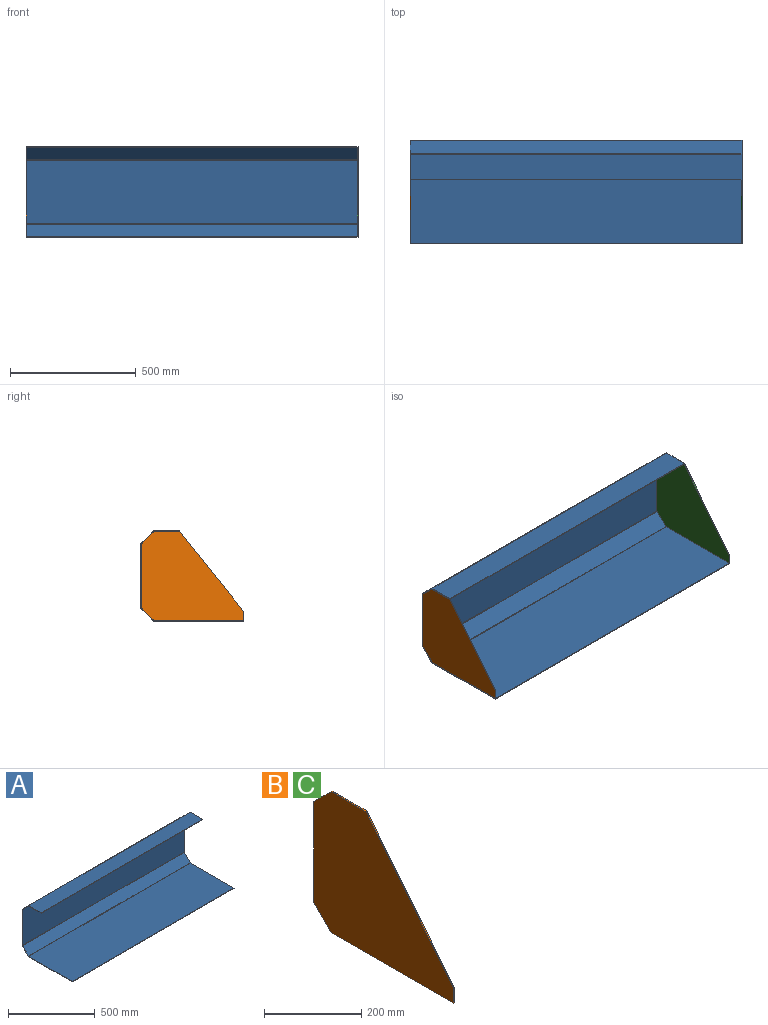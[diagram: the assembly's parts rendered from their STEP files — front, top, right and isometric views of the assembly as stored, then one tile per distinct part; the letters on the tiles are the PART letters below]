
ASSEMBLY  parts=3 mates=2
PART A: 38 faces, bbox 1320.8x409.6x362 mm
  f0: plane 354.65x3.18mm, normal (-1,0,0), area 1126mm2, adj f2,f3,f4,f35
  f1: plane 354.65x3.18mm, normal (1,0,0), area 1126mm2, adj f2,f3,f4,f34
  f2: plane 1320.8x3.18mm, normal (0,-1,0), area 4193.5mm2, adj f0,f1,f3,f4
  f3: plane 1320.8x354.65mm, normal (0,0,-1), area 468425.8mm2, adj f0,f1,f2,f36
  f4: plane 1320.8x354.65mm, normal (0,0,1), area 468425.8mm2, adj f0,f1,f2,f37
  f5: plane 252.11x3.18mm, normal (-1,0,0), area 800.4mm2, adj f7,f8,f23,f31
  f6: plane 252.11x3.18mm, normal (1,0,0), area 800.4mm2, adj f7,f8,f22,f30
  f7: plane 1320.8x252.11mm, normal (0,1,0), area 332981.9mm2, adj f5,f6,f24,f32
  f8: plane 1320.8x252.11mm, normal (0,-1,0), area 332981.9mm2, adj f5,f6,f25,f33
  f9: plane 51.71x51.71mm, normal (-1,0,0), area 222.1mm2, adj f11,f12,f19,f23
  f10: plane 51.71x51.71mm, normal (1,0,0), area 222.1mm2, adj f11,f12,f18,f22
  f11: plane 1320.8x49.46mm, normal (0,0.71,0.71), area 92387.7mm2, adj f9,f10,f20,f24
  f12: plane 1320.8x49.46mm, normal (0,-0.71,-0.71), area 92387.7mm2, adj f9,f10,f21,f25
  f13: plane 100.65x3.18mm, normal (-1,0,0), area 319.6mm2, adj f14,f16,f17,f19
  f14: plane 1320.8x3.18mm, normal (0,-1,0), area 4193.5mm2, adj f13,f15,f16,f17
  f15: plane 100.65x3.18mm, normal (1,0,0), area 319.6mm2, adj f14,f16,f17,f18
  f16: plane 1320.8x100.65mm, normal (0,0,1), area 132942.6mm2, adj f13,f14,f15,f20
  f17: plane 1320.8x100.65mm, normal (0,0,-1), area 132942.6mm2, adj f13,f14,f15,f21
  f18: plane 3.86x3.84mm, normal (1,0,0), area 9.7mm2, adj f10,f15,f20,f21
  f19: plane 3.86x3.84mm, normal (-1,0,0), area 9.7mm2, adj f9,f13,f20,f21
  f20: cylinder r=5.46mm len=1320.8mm, axis (1,0,0), area 5665mm2, adj f11,f16,f18,f19
  f21: cylinder r=2.29mm len=1320.8mm, axis (1,0,0), area 2371.4mm2, adj f12,f17,f18,f19
  f22: plane 3.86x3.84mm, normal (1,0,0), area 9.7mm2, adj f6,f10,f24,f25
  f23: plane 3.86x3.84mm, normal (-1,0,0), area 9.7mm2, adj f5,f9,f24,f25
  f24: cylinder r=5.46mm len=1320.8mm, axis (1,0,0), area 5665mm2, adj f7,f11,f22,f23
  f25: cylinder r=2.29mm len=1320.8mm, axis (1,0,0), area 2371.4mm2, adj f8,f12,f22,f23
  f26: plane 51.71x51.71mm, normal (-1,0,0), area 222.1mm2, adj f28,f29,f31,f35
  f27: plane 51.71x51.71mm, normal (1,0,0), area 222.1mm2, adj f28,f29,f30,f34
  f28: plane 1320.8x49.46mm, normal (0,0.71,-0.71), area 92387.7mm2, adj f26,f27,f32,f36
  f29: plane 1320.8x49.46mm, normal (0,-0.71,0.71), area 92387.7mm2, adj f26,f27,f33,f37
  f30: plane 3.86x3.84mm, normal (1,0,0), area 9.7mm2, adj f6,f27,f32,f33
  f31: plane 3.86x3.84mm, normal (-1,0,0), area 9.7mm2, adj f5,f26,f32,f33
  f32: cylinder r=5.46mm len=1320.8mm, axis (1,0,0), area 5665mm2, adj f7,f28,f30,f31
  f33: cylinder r=2.29mm len=1320.8mm, axis (1,0,0), area 2371.4mm2, adj f8,f29,f30,f31
  f34: plane 3.86x3.84mm, normal (1,0,0), area 9.7mm2, adj f1,f27,f36,f37
  f35: plane 3.86x3.84mm, normal (-1,0,0), area 9.7mm2, adj f0,f26,f36,f37
  f36: cylinder r=5.46mm len=1320.8mm, axis (1,0,0), area 5665mm2, adj f3,f28,f34,f35
  f37: cylinder r=2.29mm len=1320.8mm, axis (1,0,0), area 2371.4mm2, adj f4,f29,f34,f35
PART B: 9 faces, bbox 3.2x406.4x355.6 mm
  f0: plane 50.8x50.8mm, normal (0,0.71,0.71), area 228.1mm2, adj f1,f6,f7,f8
  f1: plane 254x3.18mm, normal (0,1,0), area 806.5mm2, adj f0,f2,f7,f8
  f2: plane 50.8x50.8mm, normal (0,0.71,-0.71), area 228.1mm2, adj f1,f3,f7,f8
  f3: plane 355.6x3.18mm, normal (0,0,-1), area 1129mm2, adj f2,f4,f7,f8
  f4: plane 38.1x3.18mm, normal (0,-1,0), area 121mm2, adj f3,f5,f7,f8
  f5: plane 317.5x254mm, normal (0,-0.78,0.62), area 1290.9mm2, adj f4,f6,f7,f8
  f6: plane 101.6x3.18mm, normal (0,0,1), area 322.6mm2, adj f0,f5,f7,f8
  f7: plane 406.4x355.6mm, normal (-1,0,0), area 101612.7mm2, adj f0,f1,f2,f3,f4,f5,f6
  f8: plane 406.4x355.6mm, normal (1,0,0), area 101612.7mm2, adj f0,f1,f2,f3,f4,f5,f6
PART C: same geometry as B
PLACE A t=(-9.53,0,0)mm
PLACE B t=(-669.92,0,0)mm
PLACE C t=(647.7,0,0)mm
MATE fastened A.f2 <-> C.f4  axis (0,1,0) through (650.88,-203.2,-127)mm
MATE fastened B.f4 <-> A.f2  axis (0,-1,0) through (-669.92,-203.2,-127)mm
